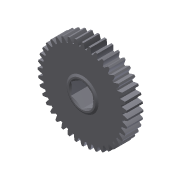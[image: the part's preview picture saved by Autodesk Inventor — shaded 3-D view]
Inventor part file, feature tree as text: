
AUTODESK INVENTOR PART (.ipt)
format: ipt  version: 2011 (Build 150239000, 239)  size: 333,824 bytes
history: native  units: mm (DEFAULTED — no unit token found)
features: sketch x5, other x4, extrude x3, plane x3, revolve x1, projected_geometry x1
ambient origin geometry x8: Origin, YZ Plane, XZ Plane, XY Plane, X Axis, Y Axis, Z Axis, Center Point
bodies: Solid1 (feature_tree)
feature tree (17):
  other  "Gear 40T 20dp 500hex"
  extrude  "Extrusion1"  Depth=9.525mm TaperAngle=0.0deg
  plane  "Work Plane1"
  plane  "Work Plane2"
  plane  "Work Plane3"
  other  "Spur Gear"
  extrude  "Extrusion2"  Depth=76.2mm TaperAngle=0.0deg
  extrude  "Extrusion3"  TaperAngle=0.0deg  [1 undecoded]
  revolve  "Revolution1"  [1 undecoded]
  sketch  "Sketch1"  dims[d0=53.34mm d1=9.525mm d2=0.0mm]
  sketch  "Sketch2"  dims[d3=50.8mm d4=76.2mm d5=0.0mm]
  other  "Srf1"
  sketch  "Sketch3"  dims[d6=0.0mm d7=0.785398mm d9=0.0mm]
  sketch  "Sketch4"  dims[d14=0.0mm d15=127.0mm d16=0.0mm]
  sketch  "Sketch5"  dims[d17=0.0mm d18=0.0mm d19=127.0mm d20=19.05mm d21=0.635mm d22=0.0mm d23=12.7mm d24=0.635mm d25=0.0mm d26=1.143mm d27=0.889mm d28=5.070181mm d29=2.54mm d30=90.0deg]
  other  "Pitch Diameter"
  projected_geometry  "Project Cut Edges1"
note: 2 required parameter values undecoded (feature->parameter linkage not recoverable at this tier; creation-order binding heuristic only, values carry confidence <= 0.55)